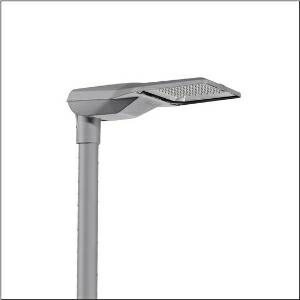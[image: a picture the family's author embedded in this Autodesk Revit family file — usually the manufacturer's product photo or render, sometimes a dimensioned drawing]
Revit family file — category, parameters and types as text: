
# Revit family: streetlight_sl_21_iq_midi___st1_5a_5xe3p31d08mb_51c0
name_source: partatom
category: Lighting Fixtures
units: mm (PartAtom-declared; Revit-internal decimal feet)

## family parameters
Cut with Voids When Loaded = No
Host = Face
Light Source = No
Part Type = Normal
Room Calculation Point = No
Round Connector Dimension = Use Diameter
Shared = No

## types (1)
- --- (1 x LED, 19170 lm, 146.7 W, 3000K)
    Apparent Load = 147 VA
    CIE Flux Codes = 22 53 95 100 100
    Color Rendering = 70
    Color Temperature = 3000K
    Default Elevation = 1800 mm
    Description = Streetlight SL 21 iQ midi, mast luminaire, primary light control with lens, of PMMA, primary optical cover: cover, of toughened safety glass, transparent, light distribution: ST1.5a, light emission: direct distribution, primary light characteristic: asymmetric, installation type: post-top, side-entry, LED, High Power LED, rated luminous flux: 19.170lm, luminous efficacy: 131lm/W, light colour: 730, colour temperature: 3000K, control gear: iQ-Comfort, control: Auto-Match, Temp-Guard, Lumen-Switch, Night-Set, Smart-Wire, Light-Fading, Desk-Remote (wireless, voltage-free reading and setting of iQ features in the workshop via application-optimized NFC function/RFID function), optimised constant luminous flux control (CLO 2.0), pre-setting: linear dimming characteristic, mains connection: 230..240V, AC, 50/60Hz, start of lifetime: 147W, end of service life: 161W, reduction: 62W, luminaire housing, of diecast aluminium, powder-coated, Siteco® metallic grey (DB 702S), corrosivity category C5 mid according to DIN EN ISO 12944, please order mast flange separately, inclination adjustable: 0°, 5°, 10°, 15°, sealing non-destructively replaceable, multi-level sealing system, length: 644mm, width: 335mm, height: 110mm, mast flange for spigot size: 42mm (side-entry): 5XC10008XM4, 60/48mm (side-entry/post-top): 5XC10108XM2, 76/60mm (side-entry/post-top): 5XC10108XM1, mounting height: 4..8m, protection rating (complete): IP66, insulation class (complete): insulation class II (safety insulation), certification: CE, ENEC, ENEC+, VDE, impact resistance: IK10, permissible operating ambient temperature for outdoor applications: -40..+50°C, standard-compliant lighting for roads and squares, packaging unit: 1 piece

Light Distribution: ST1.5a
    Height = 111 mm
    Lamp = 1 x LED
    Lamp Light Flux = 19170 lm
    Lamp Power = 146.7 W
    Lamp count = 1
    Length = 644 mm
    Luminous efficacy = 131 lm/W
    Manufacturer = Siteco
    ModVariant = No
    Model = 5XE3P31D08MB
    Number of Poles = 1
    OnlyDefault = Yes
    Power Factor = 1
    Product Name = Streetlight SL 21 iQ midi | ST1.5a
    Product group = mast luminaire | pylon top
    ProductGroupID = 6100
    Protection Class = Protection class II
    Protection Degree = IP 66
    RLX_Detail_Level = 1
    RLX_Emergency_Light_Flux = 0 lm
    RLX_Emergency_Type = 0
    RLX_Emergency_Type_DB = No
    RlxData = <blob elided: 30461 chars, md5=9c8d5b40>
    Socket = socket
    Standby Power = 0 W
    System Light Flux = 19169 lm
    System Power = 147 W
    Type Comments = factory setting: luminous flux: 100 % | dim-lin: 254 | 753 mA
    Type Image = l_1004298.jpg
    URL = http://relux.com
    VarID = @adj_197799
    Voltage = 0 V
    Weight = 0.00 kg
    Width = 336 mm

## geometry (parser evidence)
native form markers: Blend x4, Sweep x10
no freeform markers — native parametric forms only
